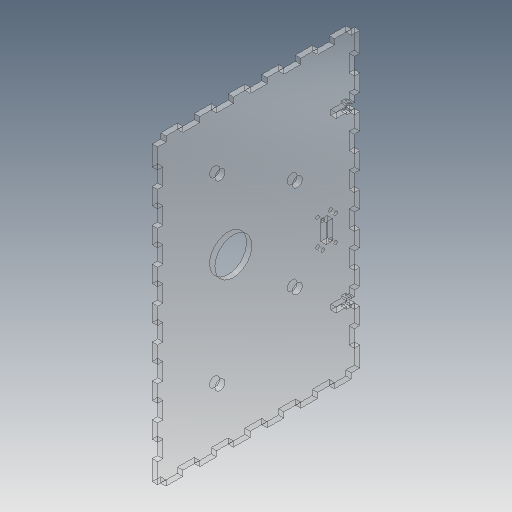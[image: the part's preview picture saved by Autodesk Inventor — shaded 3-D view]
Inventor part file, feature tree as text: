
AUTODESK INVENTOR PART (.ipt)
format: ipt  version: 2018 (Build 220112000, 112)  size: 602,112 bytes
history: native  units: mm
features: sketch x8, projected_geometry x7, extrude x6, mirror x3, hole x3, pattern_linear x2
ambient origin geometry x8: Origin, YZ Plane, XZ Plane, XY Plane, X Axis, Y Axis, Z Axis, Center Point
bodies: Solid1 (feature_tree)
feature tree (29):
  extrude  "Extrusion1"  Depth=173.65mm
  extrude  "Extrusion4"  TaperAngle=0.0deg  [1 undecoded]
  pattern_linear  "Rectangular Pattern3"  Spacing1=2.5mm  [1 undecoded]
  mirror  "Mirror3"
  extrude  "Extrusion5"  TaperAngle=60.0deg  [1 undecoded]
  pattern_linear  "Rectangular Pattern4"  Spacing1=60.0deg  [1 undecoded]
  extrude  "Extrusion8"  Depth=10.0mm
  mirror  "Mirror4"
  hole  "Hole1"  [1 undecoded]
  sketch  "Sketch6"  dims[d4=95.0mm]
  hole  "Hole6"  [1 undecoded]
  extrude  "Extrusion6"  Depth=3.175mm
  mirror  "Mirror5"
  hole  "Hole9"  [1 undecoded]
  extrude  "Extrusion7"  Depth=60.0mm
  sketch  "Sketch1"  dims[d0=113.65mm d1=173.65mm]
  sketch  "Sketch2"  dims[d2=3.175mm d3=0.0mm]
  projected_geometry  "Projected Loop1"
  projected_geometry  "Projected Loop2"
  projected_geometry  "Projected Loop5"
  sketch  "Sketch10"  dims[d5=22.0mm]
  projected_geometry  "Projected Loop6"
  sketch  "Sketch11"  dims[d6=6.0mm d7=4.0mm d8=2.0mm d9=90.0deg d10=8.0mm d11=20.594885mm]
  projected_geometry  "Projected Loop7"
  sketch  "Sketch14"  dims[d12=41.825mm]
  sketch  "Sketch15"  dims[d40=3.0mm]
  projected_geometry  "Projected Loop8"
  sketch  "Sketch16"  dims[d41=5.5mm d42=2.5mm d74=60.0deg d75=60.0deg d77=6.0mm d78=6.0mm d79=4.0mm d80=2.0mm d81=90.0deg d82=8.0mm d83=20.594885mm d84=10.0mm d85=1.825mm d86=3.175mm d87=10.0mm d88=0.0mm d89=60.0mm d91=20.0mm d92=3.175mm d94=10.0mm d95=10.0mm d96=0.0mm d97=90.0mm d99=20.0mm d100=5.0mm d101=10.825mm d103=2.0mm d104=2.0mm d105=50.0mm d106=10.0mm d107=0.0mm d127=15.24mm d128=45.72mm d129=2.156mm d130=5.69mm d131=4.0mm d132=2.0mm d133=90.0deg d134=8.865mm d135=20.594885mm d136=3.81mm d137=11.43mm d138=1.905mm d140=1.905mm d141=10.0mm d142=0.0mm d143=7.62mm d144=10.0mm d145=0.0mm]
  projected_geometry  "Projected Loop9"
note: 7 required parameter values undecoded (feature->parameter linkage not recoverable at this tier; creation-order binding heuristic only, values carry confidence <= 0.55)
